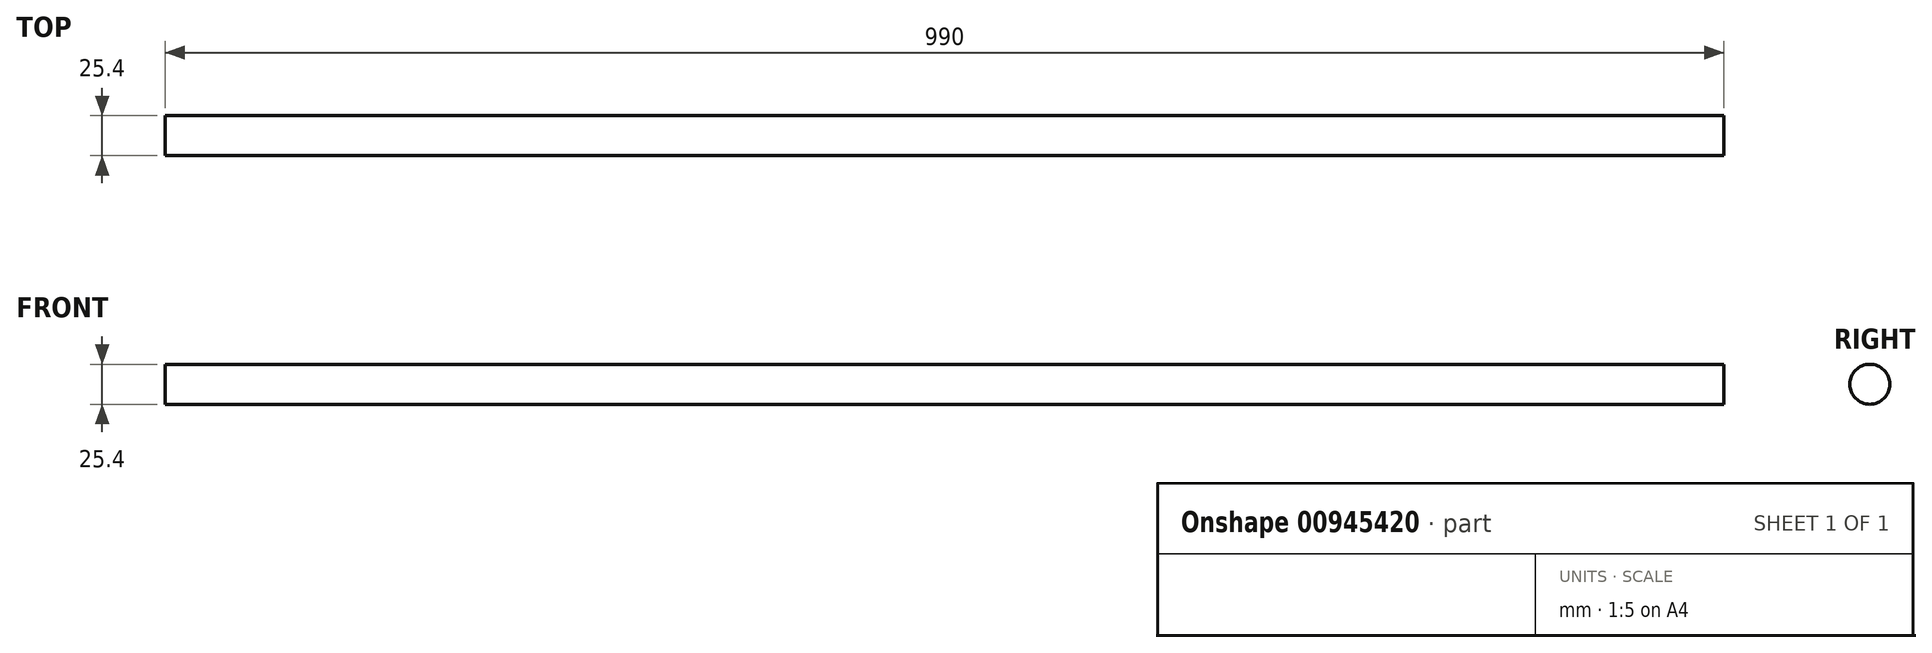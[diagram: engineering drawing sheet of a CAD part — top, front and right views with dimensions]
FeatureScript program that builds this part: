
annotation { "Feature Type Name" : "Feature", "Feature Type Description" : "" }
export const myFeature = defineFeature(function(context is Context, id is Id, definition is map)
    precondition{}
    {
        {
            var Q0;
            Q0=qCreatedBy(makeId("Right.planeOp"),FACE);
            var sketch = newSketch(context, id + "F0", { "sketchPlane" : qUnion([Q0])});
            skCircle(sketch, "E0", {"center": v(0, 0) * mm, "radius": 12.7 * mm});
            skSolve(sketch);
        }
        {
            var Q0;
            Q0=sQuery(id+"F0.wireOp",EDGE,"E0");
            extrude(context, id + "F1", {"bodyType" : ToolBodyType.SURFACE, "surfaceEntities" : qUnion([Q0]), "depth" : 990 * mm, "offsetDistance" : 25.4 * mm});
        }
    });
